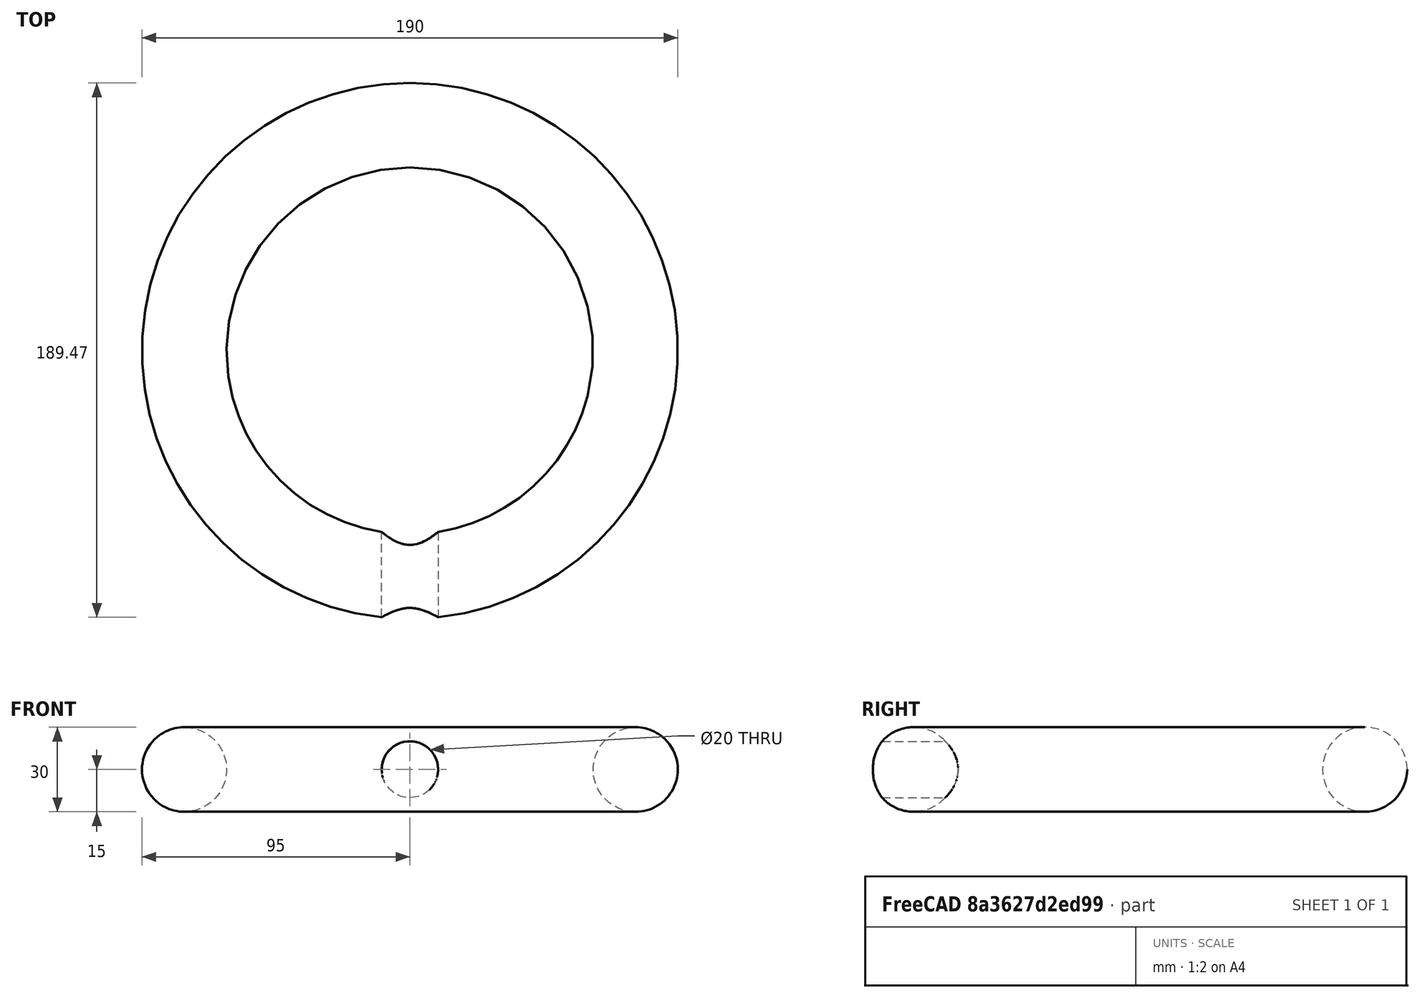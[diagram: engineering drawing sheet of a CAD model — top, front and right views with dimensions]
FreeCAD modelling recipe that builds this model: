
FCSTD DOCUMENT  (FreeCAD 0.21R33668 +26 (Git))
Label: Perçcage cylindre essai2
License: All rights reserved
LicenseURL: http://en.wikipedia.org/wiki/All_rights_reserved
objects: TechDraw::DrawProjGroupItem×6, Sketcher::SketchObject×2, TechDraw::DrawViewDimension×2, PartDesign::Revolution×1, PartDesign::Pocket×1, PartDesign::Body×1, TechDraw::DrawSVGTemplate×1, TechDraw::DrawProjGroup×1, TechDraw::DrawViewAnnotation×1, TechDraw::DrawPage×1
note: 7 computed .brp shape members not serialized (recipe doc carries the construction recipe); baked Part::Feature solids carry a one-line shape summary decoded from their .brp

FEATURE [Sketcher::SketchObject] Sketch
  FullyConstrained = true
  MapMode = 5
  Placement = pos=(0,0,0) rot=(0.57735,0.57735,0.57735;2.0944rad)
  Support = -> [YZ_Plane]
  sketch-geometry (1):
    g0: Circle CenterX=80 CenterY=0 CenterZ=0 NormalX=0 NormalY=0 NormalZ=1 AngleXU=0 Radius=15
  constraints (3):
    c: PointOnObject(g0,g-1)
    c: Radius(g0) = 15
    c: DistanceX(g-1,g0) = 80
FEATURE [PartDesign::Revolution] Revolution
  Angle = 360
  Axis = (-2e-16,3e-16,1)
  Base = (0,0,0)
  Placement = pos=(0,0,0) rot=(0.57735,0.57735,0.57735;2.0944rad)
  Profile = -> Sketch
  ReferenceAxis = -> Sketch [V_Axis]
  Reversed = true
FEATURE [Sketcher::SketchObject] Sketch001
  FullyConstrained = true
  MapMode = 5
  Placement = pos=(0,0,0) rot=(1,0,0;1.5708rad)
  Support = -> [XZ_Plane]
  sketch-geometry (1):
    g0: Circle CenterX=0 CenterY=0 CenterZ=0 NormalX=0 NormalY=0 NormalZ=1 AngleXU=0 Radius=10
  constraints (2):
    c: Coincident(g0,g-1)
    c: Radius(g0) = 10
FEATURE [PartDesign::Pocket] Pocket
  BaseFeature = -> Revolution
  Direction = (0,1,-2e-16)
  Length = 50
  Length2 = 5
  Placement = pos=(0,0,0) rot=(0.57735,0.57735,0.57735;2.0944rad)
  Profile = -> Sketch001
  ReferenceAxis = -> Sketch001 [N_Axis]
  Reversed = true
  Type = 1
FEATURE [PartDesign::Body] Body
  Group = -> [Sketch,Revolution,Sketch001,Pocket]
  Origin = -> Origin
  Tip = -> Pocket
FEATURE [TechDraw::DrawSVGTemplate] Template
  EditableTexts = Designed_by_Name=Designed by Name; Drawing_number=Drawing number; FC-Date=Date; FC-SC=Scale; FC-SH=Sheet; FC-Title=Title; Subtitle=Subtitle; Weight=Weight
  Height = 210
  Orientation = 1
  Template = C:/Program Files/FreeCAD 0.21/data/Mod/TechDraw/Templates/A4_LandscapeTD.svg
  Width = 297
FEATURE [TechDraw::DrawProjGroupItem] ProjItem  label="Front"
  CoarseView = false
  Direction = (0,0,-1)
  Focus = 100
  HardHidden = false
  IsoCount = 0
  IsoHidden = false
  IsoVisible = false
  LockPosition = true
  Perspective = false
  Rotation = 0
  RotationVector = (1,0,0)
  Scale = 0.375
  ScaleType = 2
  ScrubCount = 0
  SeamHidden = false
  SeamVisible = false
  SmoothHidden = false
  SmoothVisible = true
  Source = -> [Pocket]
  Type = 0
  X = 0
  XDirection = (1,0,0)
  Y = 0
FEATURE [TechDraw::DrawProjGroupItem] ProjItem001  label="Right"
  CoarseView = false
  Direction = (1,0,-1e-16)
  Focus = 100
  HardHidden = false
  IsoCount = 0
  IsoHidden = false
  IsoVisible = false
  LockPosition = false
  Perspective = false
  Rotation = 0
  RotationVector = (1,0,0)
  Scale = 0.375
  ScaleType = 2
  ScrubCount = 0
  SeamHidden = false
  SeamVisible = false
  SmoothHidden = false
  SmoothVisible = true
  Source = -> [Pocket]
  Type = 2
  X = -77.4633
  XDirection = (1e-16,0,1)
  Y = 0
FEATURE [TechDraw::DrawProjGroupItem] ProjItem002  label="Left"
  CoarseView = false
  Direction = (-1,0,-1e-16)
  Focus = 100
  HardHidden = false
  IsoCount = 0
  IsoHidden = false
  IsoVisible = false
  LockPosition = false
  Perspective = false
  Rotation = 0
  RotationVector = (1,0,0)
  Scale = 0.375
  ScaleType = 2
  ScrubCount = 0
  SeamHidden = false
  SeamVisible = false
  SmoothHidden = false
  SmoothVisible = true
  Source = -> [Pocket]
  Type = 1
  X = 56.25
  XDirection = (1e-16,0,-1)
  Y = 0
FEATURE [TechDraw::DrawProjGroupItem] ProjItem003  label="Bottom"
  CoarseView = false
  Direction = (0,1,0)
  Focus = 100
  HardHidden = false
  IsoCount = 0
  IsoHidden = false
  IsoVisible = false
  LockPosition = false
  Perspective = false
  Rotation = 0
  RotationVector = (1,0,0)
  Scale = 0.375
  ScaleType = 2
  ScrubCount = 0
  SeamHidden = false
  SeamVisible = false
  SmoothHidden = false
  SmoothVisible = true
  Source = -> [Pocket]
  Type = 5
  X = 0
  XDirection = (1,0,0)
  Y = 83.5374
FEATURE [TechDraw::DrawProjGroupItem] ProjItem004  label="Top"
  CoarseView = false
  Direction = (0,-1,0)
  Focus = 100
  HardHidden = false
  IsoCount = 0
  IsoHidden = false
  IsoVisible = false
  LockPosition = false
  Perspective = false
  Rotation = 0
  RotationVector = (1,0,0)
  Scale = 0.375
  ScaleType = 2
  ScrubCount = 0
  SeamHidden = false
  SeamVisible = false
  SmoothHidden = false
  SmoothVisible = true
  Source = -> [Pocket]
  Type = 4
  X = 0
  XDirection = (1,0,0)
  Y = -56.151
FEATURE [TechDraw::DrawProjGroupItem] ProjItem005  label="FrontBottomRight"
  CoarseView = false
  Direction = (0.57735,0.57735,-0.57735)
  Focus = 100
  HardHidden = false
  IsoCount = 0
  IsoHidden = false
  IsoVisible = false
  LockPosition = false
  Perspective = false
  Rotation = 0
  RotationVector = (1,0,0)
  Scale = 0.375
  ScaleType = 2
  ScrubCount = 0
  SeamHidden = false
  SeamVisible = false
  SmoothHidden = false
  SmoothVisible = true
  Source = -> [Pocket]
  Type = 9
  X = -77.4633
  XDirection = (0.707107,0,0.707107)
  Y = 83.5374
FEATURE [TechDraw::DrawProjGroup] ProjGroup
  Anchor = -> ProjItem
  AutoDistribute = true
  LockPosition = false
  ProjectionType = 0
  Rotation = 0
  Scale = 0.375
  ScaleType = 1
  Source = -> [Pocket]
  Views = -> [ProjItem,ProjItem001,ProjItem002,ProjItem003,ProjItem004,ProjItem005]
  X = 148.5
  Y = 105
  spacingX = 15
  spacingY = 15
FEATURE [TechDraw::DrawViewDimension] Dimension
  AngleOverride = false
  Arbitrary = false
  ArbitraryTolerances = false
  EqualTolerance = true
  ExtensionAngle = 0
  FormatSpec = %.2w
  FormatSpecOverTolerance = %+.2w
  FormatSpecUnderTolerance = %+.2w
  Inverted = false
  LineAngle = 0
  LockPosition = false
  MeasureType = 1
  OverTolerance = 0
  References2D = -> [ProjItem001]
  Rotation = 0
  Scale = 0.8
  ScaleType = 0
  TheoreticalExact = false
  Type = 1
  UnderTolerance = 0
  X = 0
  Y = 2.5
FEATURE [TechDraw::DrawViewDimension] Dimension001
  AngleOverride = false
  Arbitrary = false
  ArbitraryTolerances = false
  EqualTolerance = true
  ExtensionAngle = 0
  FormatSpec = R%.2w
  FormatSpecOverTolerance = %+.2w
  FormatSpecUnderTolerance = %+.2w
  Inverted = false
  LineAngle = 0
  LockPosition = false
  MeasureType = 1
  OverTolerance = 0
  References2D = -> [ProjItem]
  Rotation = 0
  Scale = 0.8
  ScaleType = 0
  TheoreticalExact = false
  Type = 4
  UnderTolerance = 0
  X = -49.3975
  Y = -7.26434
FEATURE [TechDraw::DrawViewAnnotation] Annotation
  Font = osifont
  LineSpace = 100
  LockPosition = false
  MaxWidth = -1
  Rotation = 0
  Scale = 0.8
  ScaleType = 0
  Text = Default Text
  TextSize = 5
  TextStyle = 0
  X = 148.5
  Y = 105
FEATURE [TechDraw::DrawPage] Page
  KeepUpdated = true
  NextBalloonIndex = 1
  ProjectionType = 0
  Scale = 0.8
  Template = -> Template
  Views = -> [ProjGroup,Dimension,Dimension001,Annotation]
